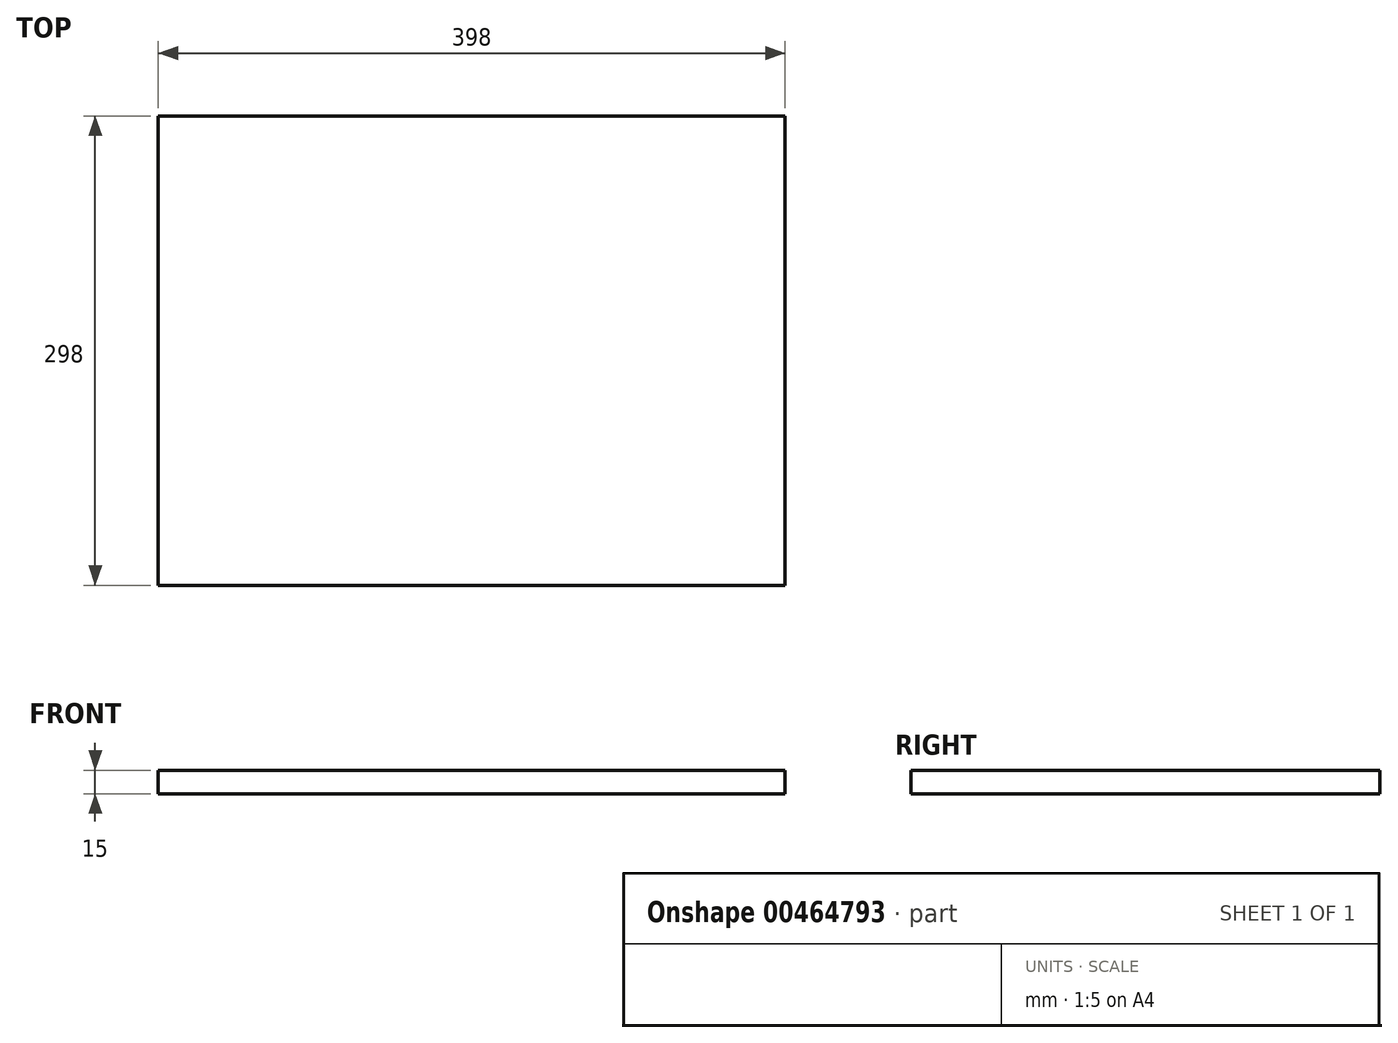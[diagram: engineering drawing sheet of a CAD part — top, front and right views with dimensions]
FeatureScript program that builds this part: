
annotation { "Feature Type Name" : "Feature", "Feature Type Description" : "" }
export const myFeature = defineFeature(function(context is Context, id is Id, definition is map)
    precondition{}
    {
        {
            var Q0;
            Q0=qCreatedBy(makeId("Top.planeOp"),FACE);
            var sketch = newSketch(context, id + "F0", { "sketchPlane" : qUnion([Q0])});
            skLineSegment(sketch, "E0.bottom", {"start": v(0, 0) * mm, "end": v(398, 0) * mm});
            skLineSegment(sketch, "E0.top", {"start": v(0, 298) * mm, "end": v(398, 298) * mm});
            skLineSegment(sketch, "E0.left", {"start": v(0, 0) * mm, "end": v(0, 298) * mm});
            skLineSegment(sketch, "E0.right", {"start": v(398, 0) * mm, "end": v(398, 298) * mm});
            skSolve(sketch);
        }
        {
            var Q0;
            Q0 = qSketchRegion(id + "F0", true);
            extrude(context, id + "F1", {"entities" : qUnion([Q0]), "depth" : 15 * mm});
        }
    });
